# Revit family: Domotics-DomesticRanges-GEWISS-27COMBI_SYSTEM-IP55_IR_MOVEMENT_DETECTOR
name_source: partatom
category: Modelli generici
revit_build: Autodesk Revit 2016 (Build: 20161004_0715(x64)
units: mm (PartAtom-declared; Revit-internal decimal feet)

## family parameters
Condiviso = No
Host = Muro
Punto di calcolo locali = No
Può ospitare armatura = No
Quota connettore circolare = Usa diametro
Sempre verticale = Sì
Taglio con vuoti quando caricato = No
Tipo di parte = Normale

## types (1)
- GW27431B - IR movement detector IP55-230V
    Catalogue = DOMOTICS
    Catalogue Range = 27COMBI
    Descrizione = IR MOVEMENT DETECTOR IP55-230V
    Duration adjustment = 5 sec. - 12 min.
    EAN code = 8011564825338
    Electrocod = 0143
    Glow Wire Test = 650°C
    IDF = 5de224fa-22b0-46fc-80e2-1b54ddaa2f1e
    IDT = 666a0526-0741-48d4-9456-c3f3148265d2
    IP degree = IP55
    Immagine tipo = GW27431B.jpg
    Installation temperature = -25 +60 °C
    Insulation class = II
    Modello = GW27431B
    Outer dim. LxHxD (mm) = 72x88x106
    Produttore = GEWISS S.p.A.
    Range of action = 12m
    Standard = EN 60669-2-1
    Technical sheet = https://www.gewiss.com
    Thermo-pressure with ball = 70
    Treshold adjustment = 5 - 1000 lux
    URL = https://www.gewiss.com
    Version file RFA = 18.0

note: source unit labels omitted for Thermo-pressure with ball — the stored unit's dimension contradicts the parameter name (converter mislabeling)

## geometry (parser evidence)
native form markers: Sweep x1
no freeform markers — native parametric forms only
